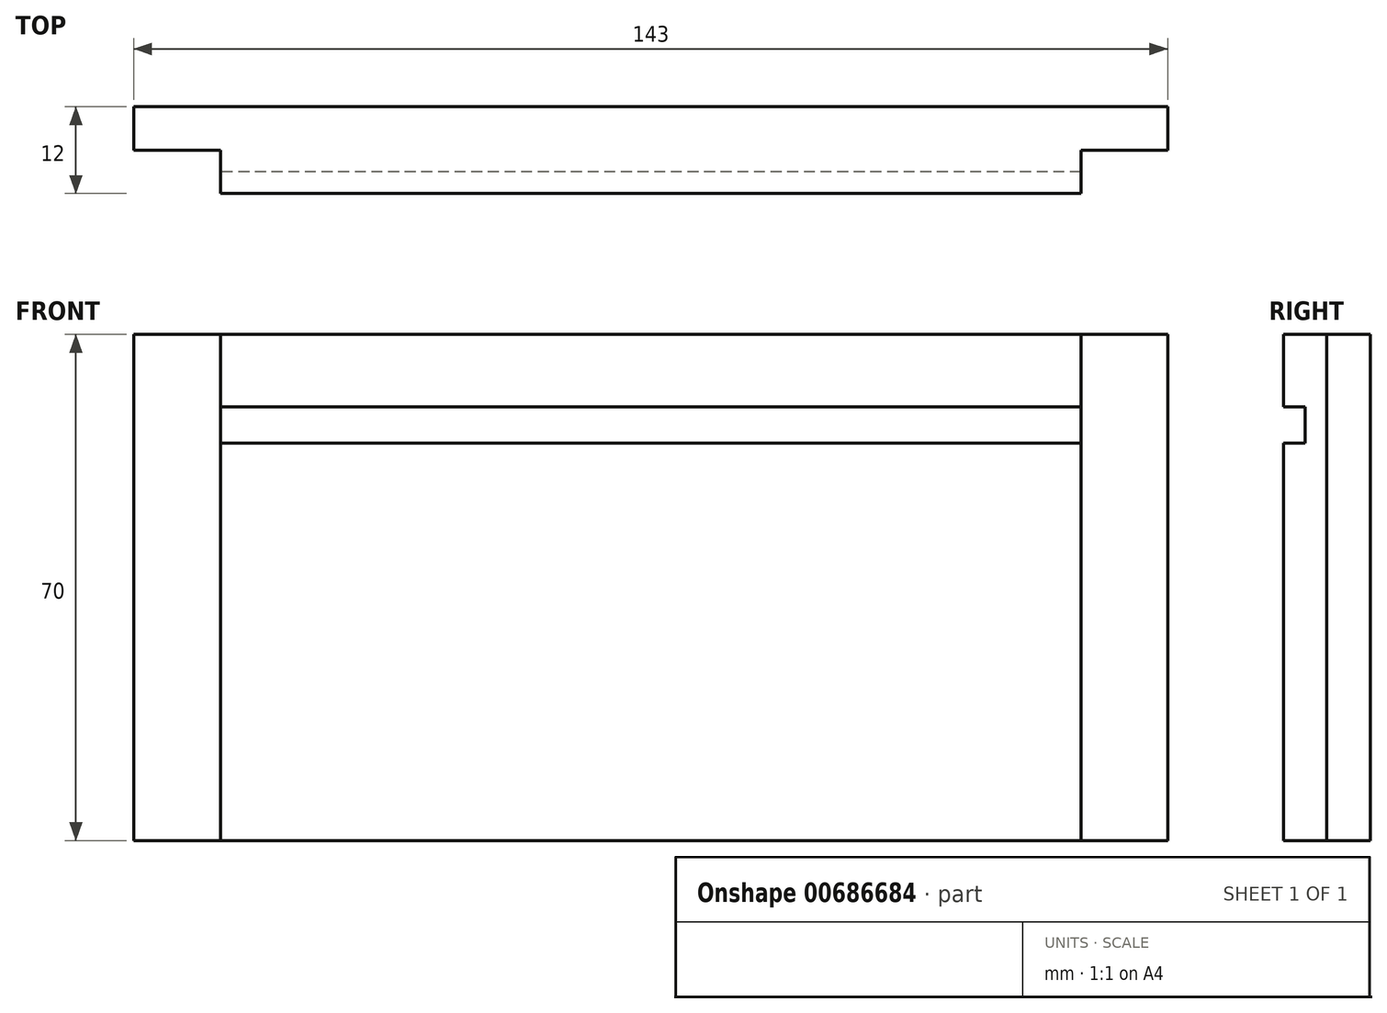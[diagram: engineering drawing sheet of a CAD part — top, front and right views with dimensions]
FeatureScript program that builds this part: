
annotation { "Feature Type Name" : "Feature", "Feature Type Description" : "" }
export const myFeature = defineFeature(function(context is Context, id is Id, definition is map)
    precondition{}
    {
        {
            var Q0;
            Q0=qCreatedBy(makeId("Right.planeOp"),FACE);
            var sketch = newSketch(context, id + "F0", { "sketchPlane" : qUnion([Q0])});
            skLineSegment(sketch, "E0", {"start": v(0, 0) * mm, "end": v(0, 70) * mm});
            skLineSegment(sketch, "E1", {"start": v(0, 70) * mm, "end": v(-12, 70) * mm});
            skLineSegment(sketch, "E2", {"start": v(-12, 70) * mm, "end": v(-12, 60) * mm});
            skLineSegment(sketch, "E3", {"start": v(-9, 60) * mm, "end": v(-12, 60) * mm});
            skLineSegment(sketch, "E4", {"start": v(-9, 60) * mm, "end": v(-9, 55) * mm});
            skLineSegment(sketch, "E5", {"start": v(-9, 55) * mm, "end": v(-12, 55) * mm});
            skLineSegment(sketch, "E6", {"start": v(-12, 55) * mm, "end": v(-12, 0) * mm});
            skLineSegment(sketch, "E7", {"start": v(-12, 0) * mm, "end": v(0, 0) * mm});
            skSolve(sketch);
        }
        {
            var Q0;
            Q0=qSketchRegion(id+"F0",true);
            extrude(context, id + "F1", {"entities" : qUnion([Q0]), "depth" : 143 * mm, "offsetDistance" : 25 * mm});
        }
        {
            var Q0;
            Q0=makeQuery(id+"F1.opExtrude","SWEPT_FACE",FACE,{"disambiguationData":[OSD([sQuery(id+"F0.wireOp",EDGE,"E6")])]});
            var sketch = newSketch(context, id + "F2", { "sketchPlane" : qUnion([Q0])});
            skLineSegment(sketch, "E8.bottom", {"start": v(143, 0) * mm, "end": v(131, 0) * mm});
            skLineSegment(sketch, "E8.top", {"start": v(143, 70) * mm, "end": v(131, 70) * mm});
            skLineSegment(sketch, "E8.left", {"start": v(143, 0) * mm, "end": v(143, 70) * mm});
            skLineSegment(sketch, "E8.right", {"start": v(131, 0) * mm, "end": v(131, 70) * mm});
            skLineSegment(sketch, "E9.bottom", {"start": v(0, 0) * mm, "end": v(12, 0) * mm});
            skLineSegment(sketch, "E9.top", {"start": v(0, 70) * mm, "end": v(12, 70) * mm});
            skLineSegment(sketch, "E9.left", {"start": v(0, 0) * mm, "end": v(0, 70) * mm});
            skLineSegment(sketch, "E9.right", {"start": v(12, 0) * mm, "end": v(12, 70) * mm});
            skSolve(sketch);
        }
        {
            var Q0;
            Q0=qSketchRegion(id+"F2",true);
            extrude(context, id + "F3", {"entities" : qUnion([Q0]), "operationType" : NewBodyOperationType.REMOVE, "oppositeDirection" : true, "depth" : 6 * mm, "offsetDistance" : 25 * mm});
        }
    });
